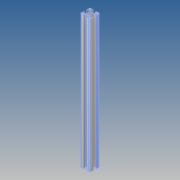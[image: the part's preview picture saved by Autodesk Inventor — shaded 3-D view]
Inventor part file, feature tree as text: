
AUTODESK INVENTOR PART (.ipt)
format: ipt  version: 2018.2 (Build 222227000, 227)  size: 224,768 bytes
history: native  units: mm
features: other x2, extrude x1
ambient origin geometry x8: Origin, YZ Plane, XZ Plane, XY Plane, X Axis, Y Axis, Z Axis, Center Point
bodies: Volumenkörper1 (feature_tree)
feature tree (3):
  other  "90-50-PROFILES-30x30xX.ipt"
  extrude  "Extrusion1"  Depth=10.0mm
  other  "Profil_Skizze"
